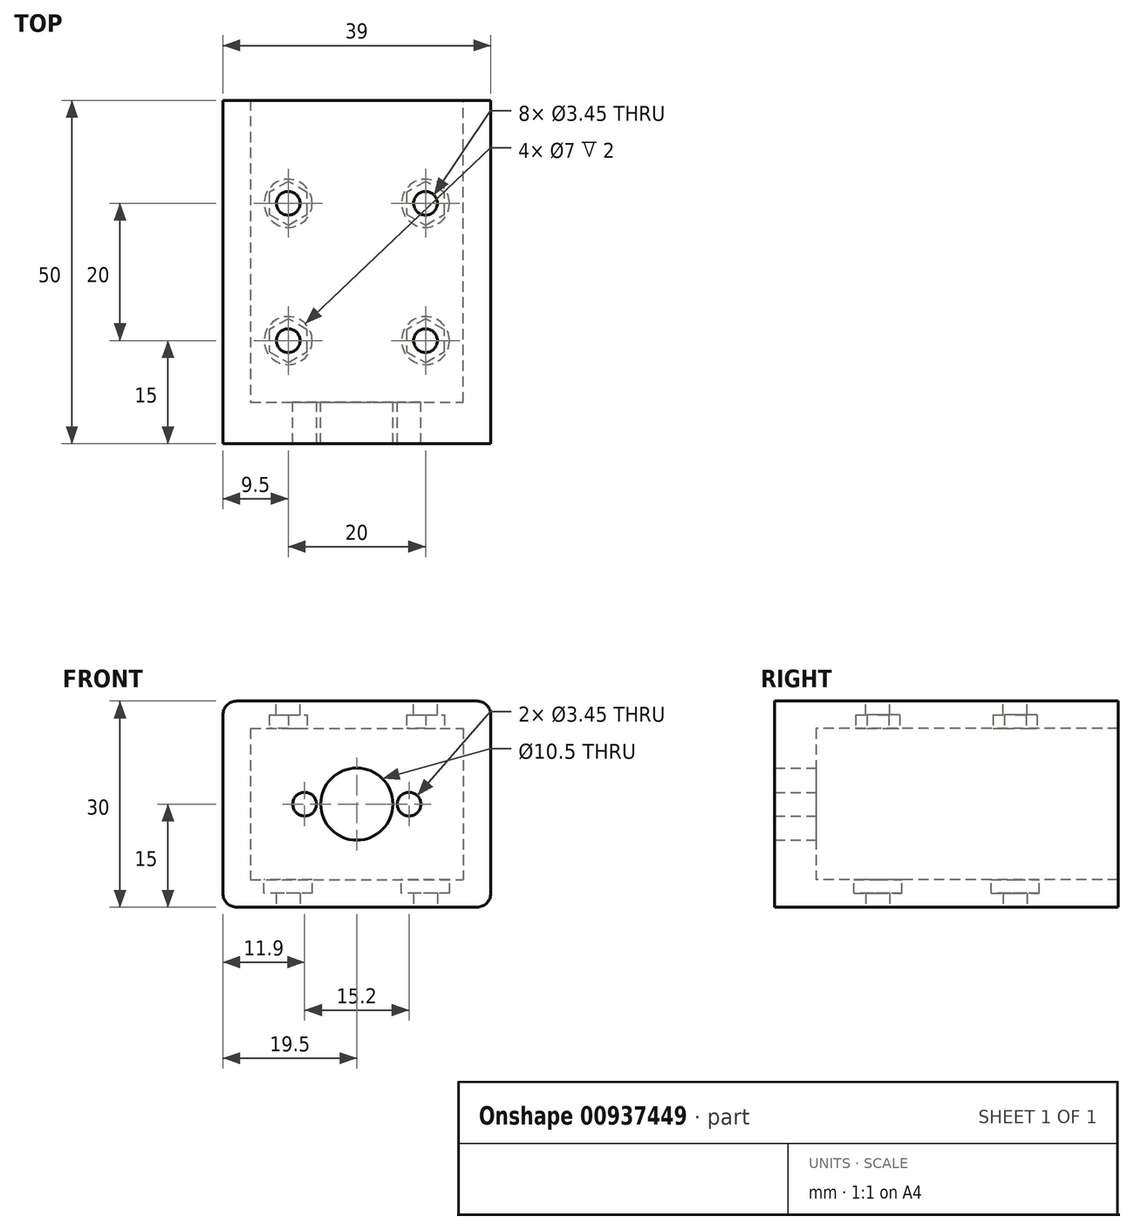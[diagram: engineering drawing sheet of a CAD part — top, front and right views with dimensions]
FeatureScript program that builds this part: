
annotation { "Feature Type Name" : "Feature", "Feature Type Description" : "" }
export const myFeature = defineFeature(function(context is Context, id is Id, definition is map)
    precondition{}
    {
        {
            var Q0;
            Q0=qCreatedBy(makeId("Top.planeOp"),FACE);
            var sketch = newSketch(context, id + "F0", { "sketchPlane" : qUnion([Q0])});
            skLineSegment(sketch, "E0.bottom", {"start": v(0, 0) * mm, "end": v(39, 0) * mm});
            skLineSegment(sketch, "E0.top", {"start": v(0, 50) * mm, "end": v(39, 50) * mm});
            skLineSegment(sketch, "E0.left", {"start": v(0, 0) * mm, "end": v(0, 50) * mm});
            skLineSegment(sketch, "E0.right", {"start": v(39, 0) * mm, "end": v(39, 50) * mm});
            skLineSegment(sketch, "E1.bottom", {"start": v(9.5, 15) * mm, "end": v(29.5, 15) * mm, "construction": true});
            skLineSegment(sketch, "E1.top", {"start": v(9.5, 35) * mm, "end": v(29.5, 35) * mm, "construction": true});
            skLineSegment(sketch, "E1.left", {"start": v(9.5, 15) * mm, "end": v(9.5, 35) * mm, "construction": true});
            skLineSegment(sketch, "E1.right", {"start": v(29.5, 15) * mm, "end": v(29.5, 35) * mm, "construction": true});
            skCircle(sketch, "E2", {"center": v(9.5, 35) * mm, "radius": 1.73 * mm});
            skCircle(sketch, "E3", {"center": v(29.5, 35) * mm, "radius": 1.73 * mm});
            skCircle(sketch, "E4", {"center": v(29.5, 15) * mm, "radius": 1.73 * mm});
            skCircle(sketch, "E5", {"center": v(9.5, 15) * mm, "radius": 1.73 * mm});
            skCircle(sketch, "E6", {"center": v(9.5, 35) * mm, "radius": 3.5 * mm});
            skCircle(sketch, "E7", {"center": v(29.5, 35) * mm, "radius": 3.5 * mm});
            skCircle(sketch, "E8", {"center": v(29.5, 15) * mm, "radius": 3.5 * mm});
            skCircle(sketch, "E9", {"center": v(9.5, 15) * mm, "radius": 3.5 * mm});
            skLineSegment(sketch, "E10", {"start": v(19.5, 0) * mm, "end": v(19.5, 15) * mm, "construction": true});
            skLineSegment(sketch, "E11", {"start": v(0, 25) * mm, "end": v(9.5, 25) * mm, "construction": true});
            skSolve(sketch);
        }
        {
            var Q0;
            Q0 = qSketchRegion(id + "F0", true);
            var Q1;
            Q1=makeQuery(id+"F0.imprint","IMPRINT",FACE,{"disambiguationData":[TD([[makeQuery(id+"F0.imprint","IMPRINT",EDGE,{"derivedFrom":sQuery(id+"F0.wireOp",EDGE,"E2")}),-1.0]])]});
            var Q2;
            Q2=makeQuery(id+"F0.imprint","IMPRINT",FACE,{"disambiguationData":[TD([[makeQuery(id+"F0.imprint","IMPRINT",EDGE,{"derivedFrom":sQuery(id+"F0.wireOp",EDGE,"E3")}),-1.0]])]});
            var Q3;
            Q3=makeQuery(id+"F0.imprint","IMPRINT",FACE,{"disambiguationData":[TD([[makeQuery(id+"F0.imprint","IMPRINT",EDGE,{"derivedFrom":sQuery(id+"F0.wireOp",EDGE,"E4")}),-1.0]])]});
            var Q4;
            Q4=makeQuery(id+"F0.imprint","IMPRINT",FACE,{"disambiguationData":[TD([[makeQuery(id+"F0.imprint","IMPRINT",EDGE,{"derivedFrom":sQuery(id+"F0.wireOp",EDGE,"E5")}),-1.0]])]});
            extrude(context, id + "F1", {"entities" : qUnion([Q0, Q1, Q2, Q3, Q4]), "depth" : 4 * mm, "offsetDistance" : 25 * mm});
        }
        {
            var Q0;
            Q0=makeQuery(id+"F1.opExtrude","CAP_FACE",FACE,{"disambiguationData":[OSD([sQuery(id+"F0.wireOp",EDGE,"E0.bottom"),sQuery(id+"F0.wireOp",EDGE,"E0.top"),sQuery(id+"F0.wireOp",EDGE,"E0.left"),sQuery(id+"F0.wireOp",EDGE,"E0.right"),sQuery(id+"F0.wireOp",EDGE,"E2"),sQuery(id+"F0.wireOp",EDGE,"E3"),sQuery(id+"F0.wireOp",EDGE,"E4"),sQuery(id+"F0.wireOp",EDGE,"E5")])],"isStart":false});
            var sketch = newSketch(context, id + "F2", { "sketchPlane" : qUnion([Q0])});
            skCircle(sketch, "E12", {"center": v(9.5, 35) * mm, "radius": 3.5 * mm});
            skCircle(sketch, "E13", {"center": v(29.5, 35) * mm, "radius": 3.5 * mm});
            skCircle(sketch, "E14", {"center": v(29.5, 15) * mm, "radius": 3.5 * mm});
            skCircle(sketch, "E15", {"center": v(9.5, 15) * mm, "radius": 3.5 * mm});
            skSolve(sketch);
        }
        {
            var Q0;
            Q0 = qSketchRegion(id + "F2", true);
            extrude(context, id + "F3", {"entities" : qUnion([Q0]), "operationType" : NewBodyOperationType.REMOVE, "oppositeDirection" : true, "depth" : 2 * mm, "offsetDistance" : 25 * mm});
        }
        {
            var Q0;
            Q0=makeQuery(id+"F1.opExtrude","CAP_FACE",FACE,{"disambiguationData":[OSD([sQuery(id+"F0.wireOp",EDGE,"E0.bottom"),sQuery(id+"F0.wireOp",EDGE,"E0.top"),sQuery(id+"F0.wireOp",EDGE,"E0.left"),sQuery(id+"F0.wireOp",EDGE,"E0.right"),sQuery(id+"F0.wireOp",EDGE,"E2"),sQuery(id+"F0.wireOp",EDGE,"E3"),sQuery(id+"F0.wireOp",EDGE,"E4"),sQuery(id+"F0.wireOp",EDGE,"E5")])],"isStart":false});
            var sketch = newSketch(context, id + "F4", { "sketchPlane" : qUnion([Q0])});
            skLineSegment(sketch, "E16", {"start": v(0, 50) * mm, "end": v(4, 50) * mm});
            skLineSegment(sketch, "E17", {"start": v(4, 50) * mm, "end": v(4, 6) * mm});
            skLineSegment(sketch, "E18", {"start": v(4, 6) * mm, "end": v(35, 6) * mm});
            skLineSegment(sketch, "E19", {"start": v(35, 6) * mm, "end": v(35, 50) * mm});
            skLineSegment(sketch, "E20", {"start": v(35, 50) * mm, "end": v(39, 50) * mm});
            skLineSegment(sketch, "E21", {"start": v(39, 50) * mm, "end": v(39, 0) * mm});
            skLineSegment(sketch, "E22", {"start": v(39, 0) * mm, "end": v(0, 0) * mm});
            skLineSegment(sketch, "E23", {"start": v(0, 0) * mm, "end": v(0, 50) * mm});
            skSolve(sketch);
        }
        {
            var Q0;
            Q0 = qSketchRegion(id + "F4", true);
            extrude(context, id + "F5", {"entities" : qUnion([Q0]), "operationType" : NewBodyOperationType.ADD, "depth" : 22 * mm, "offsetDistance" : 25 * mm});
        }
        {
            var Q0;
            Q0=makeQuery(id+"F5.opExtrude","SWEPT_FACE",FACE,{"disambiguationData":[OSD([sQuery(id+"F4.wireOp",EDGE,"E18")])]});
            var sketch = newSketch(context, id + "F6", { "sketchPlane" : qUnion([Q0])});
            skLineSegment(sketch, "E24", {"start": v(-19.5, 4) * mm, "end": v(-19.5, 15) * mm, "construction": true});
            skCircle(sketch, "E25", {"center": v(-19.5, 15) * mm, "radius": 5.25 * mm});
            skLineSegment(sketch, "E26", {"start": v(-19.5, 15) * mm, "end": v(-27.1, 15) * mm, "construction": true});
            skCircle(sketch, "E27", {"center": v(-27.1, 15) * mm, "radius": 1.73 * mm});
            skCircle(sketch, "E28", {"center": v(-11.9, 15) * mm, "radius": 1.73 * mm});
            skSolve(sketch);
        }
        {
            var Q0;
            Q0 = qSketchRegion(id + "F6", true);
            extrude(context, id + "F7", {"entities" : qUnion([Q0]), "operationType" : NewBodyOperationType.REMOVE, "endBound" : BoundingType.UP_TO_NEXT, "oppositeDirection" : true, "depth" : 25 * mm, "offsetDistance" : 25 * mm});
        }
        {
            var Q0;
            Q0=makeQuery(id+"F5.opExtrude","CAP_FACE",FACE,{"disambiguationData":[OSD([sQuery(id+"F4.wireOp",EDGE,"E16"),sQuery(id+"F4.wireOp",EDGE,"E17"),sQuery(id+"F4.wireOp",EDGE,"E18"),sQuery(id+"F4.wireOp",EDGE,"E19"),sQuery(id+"F4.wireOp",EDGE,"E20"),sQuery(id+"F4.wireOp",EDGE,"E21"),sQuery(id+"F4.wireOp",EDGE,"E22"),sQuery(id+"F4.wireOp",EDGE,"E23")])],"isStart":false});
            var sketch = newSketch(context, id + "F8", { "sketchPlane" : qUnion([Q0])});
            skLineSegment(sketch, "E29.bottom", {"start": v(0, 0) * mm, "end": v(39, 0) * mm});
            skLineSegment(sketch, "E29.top", {"start": v(0, 50) * mm, "end": v(39, 50) * mm});
            skLineSegment(sketch, "E29.left", {"start": v(0, 0) * mm, "end": v(0, 50) * mm});
            skLineSegment(sketch, "E29.right", {"start": v(39, 0) * mm, "end": v(39, 50) * mm});
            skSolve(sketch);
        }
        {
            var Q0;
            Q0 = qSketchRegion(id + "F8", true);
            extrude(context, id + "F9", {"entities" : qUnion([Q0]), "operationType" : NewBodyOperationType.ADD, "depth" : 4 * mm, "offsetDistance" : 25 * mm});
        }
        {
            var Q0;
            Q0=makeQuery(id+"F9.opExtrude","CAP_EDGE",EDGE,{"disambiguationData":[OSD([sQuery(id+"F8.wireOp",EDGE,"E29.left")])],"isStart":false});
            var Q1;
            Q1=makeQuery(id+"F1.opExtrude","CAP_EDGE",EDGE,{"disambiguationData":[OSD([sQuery(id+"F0.wireOp",EDGE,"E0.left")])],"isStart":true});
            var Q2;
            Q2=makeQuery(id+"F1.opExtrude","CAP_EDGE",EDGE,{"disambiguationData":[OSD([sQuery(id+"F0.wireOp",EDGE,"E0.right")])],"isStart":true});
            var Q3;
            Q3=makeQuery(id+"F9.opExtrude","CAP_EDGE",EDGE,{"disambiguationData":[OSD([sQuery(id+"F8.wireOp",EDGE,"E29.right")])],"isStart":false});
            var Q4;
            Q4=makeQuery(id+"F5.opExtrude","CAP_EDGE",EDGE,{"disambiguationData":[OSD([sQuery(id+"F4.wireOp",EDGE,"E19")])],"isStart":false});
            var Q5;
            Q5=makeQuery(id+"F5.opExtrude","CAP_EDGE",EDGE,{"disambiguationData":[OSD([sQuery(id+"F4.wireOp",EDGE,"E17")])],"isStart":false});
            var Q6;
            Q6=makeQuery(id+"F5.opExtrude","CAP_EDGE",EDGE,{"disambiguationData":[OSD([sQuery(id+"F4.wireOp",EDGE,"E17")])],"isStart":true});
            var Q7;
            Q7=makeQuery(id+"F5.opExtrude","CAP_EDGE",EDGE,{"disambiguationData":[OSD([sQuery(id+"F4.wireOp",EDGE,"E19")])],"isStart":true});
            fillet(context, id + "F10", {"entities" : qUnion([Q0, Q1, Q2, Q3, Q4, Q5, Q6, Q7]), "radius" : 2 * mm, "tangentPropagation" : true, "allowEdgeOverflow" : false});
        }
        {
            var Q0;
            Q0=makeQuery(id+"F9.opExtrude","CAP_FACE",FACE,{"disambiguationData":[OSD([sQuery(id+"F8.wireOp",EDGE,"E29.bottom"),sQuery(id+"F8.wireOp",EDGE,"E29.top"),sQuery(id+"F8.wireOp",EDGE,"E29.left"),sQuery(id+"F8.wireOp",EDGE,"E29.right")])],"isStart":false});
            var sketch = newSketch(context, id + "F11", { "sketchPlane" : qUnion([Q0])});
            skLineSegment(sketch, "E30.bottom", {"start": v(9.5, 35) * mm, "end": v(29.5, 35) * mm, "construction": true});
            skLineSegment(sketch, "E30.top", {"start": v(9.5, 15) * mm, "end": v(29.5, 15) * mm, "construction": true});
            skLineSegment(sketch, "E30.left", {"start": v(9.5, 35) * mm, "end": v(9.5, 15) * mm, "construction": true});
            skLineSegment(sketch, "E30.right", {"start": v(29.5, 35) * mm, "end": v(29.5, 15) * mm, "construction": true});
            skLineSegment(sketch, "E31", {"start": v(2, 25) * mm, "end": v(9.5, 25) * mm, "construction": true});
            skLineSegment(sketch, "E32", {"start": v(19.5, 15) * mm, "end": v(19.5, 0) * mm, "construction": true});
            skCircle(sketch, "E33", {"center": v(9.5, 35) * mm, "radius": 1.73 * mm});
            skCircle(sketch, "E34", {"center": v(29.5, 35) * mm, "radius": 1.73 * mm});
            skCircle(sketch, "E35", {"center": v(29.5, 15) * mm, "radius": 1.73 * mm});
            skCircle(sketch, "E36", {"center": v(9.5, 15) * mm, "radius": 1.73 * mm});
            skSolve(sketch);
        }
        {
            var Q0;
            Q0 = qSketchRegion(id + "F11", true);
            extrude(context, id + "F12", {"entities" : qUnion([Q0]), "operationType" : NewBodyOperationType.REMOVE, "endBound" : BoundingType.UP_TO_NEXT, "oppositeDirection" : true, "depth" : 25 * mm, "offsetDistance" : 25 * mm});
        }
        {
            var Q0;
            Q0=makeQuery(id+"F9.opExtrude","CAP_FACE",FACE,{"disambiguationData":[OSD([sQuery(id+"F8.wireOp",EDGE,"E29.bottom"),sQuery(id+"F8.wireOp",EDGE,"E29.top"),sQuery(id+"F8.wireOp",EDGE,"E29.left"),sQuery(id+"F8.wireOp",EDGE,"E29.right")])],"isStart":true});
            var sketch = newSketch(context, id + "F13", { "sketchPlane" : qUnion([Q0])});
            skCircle(sketch, "E37.cCircle", {"center": v(9.5, -15) * mm, "radius": 2.76 * mm, "construction": true});
            skLineSegment(sketch, "E37.0", {"start": v(9.5, -11.81) * mm, "end": v(12.26, -13.4) * mm});
            skLineSegment(sketch, "E37.1", {"start": v(12.26, -13.4) * mm, "end": v(12.26, -16.6) * mm});
            skLineSegment(sketch, "E37.2", {"start": v(12.26, -16.6) * mm, "end": v(9.5, -18.19) * mm});
            skLineSegment(sketch, "E37.3", {"start": v(9.5, -18.19) * mm, "end": v(6.74, -16.6) * mm});
            skLineSegment(sketch, "E37.4", {"start": v(6.74, -16.6) * mm, "end": v(6.74, -13.4) * mm});
            skLineSegment(sketch, "E37.5", {"start": v(6.74, -13.4) * mm, "end": v(9.5, -11.81) * mm});
            skPoint(sketch, "E37.0.midPoint", {"position": v(10.88, -12.6) * mm});
            skCircle(sketch, "E38.cCircle", {"center": v(29.5, -15) * mm, "radius": 2.76 * mm, "construction": true});
            skLineSegment(sketch, "E38.0", {"start": v(29.5, -11.81) * mm, "end": v(32.26, -13.4) * mm});
            skLineSegment(sketch, "E38.1", {"start": v(32.26, -13.4) * mm, "end": v(32.26, -16.6) * mm});
            skLineSegment(sketch, "E38.2", {"start": v(32.26, -16.6) * mm, "end": v(29.5, -18.19) * mm});
            skLineSegment(sketch, "E38.3", {"start": v(29.5, -18.19) * mm, "end": v(26.74, -16.6) * mm});
            skLineSegment(sketch, "E38.4", {"start": v(26.74, -16.6) * mm, "end": v(26.74, -13.4) * mm});
            skLineSegment(sketch, "E38.5", {"start": v(26.74, -13.4) * mm, "end": v(29.5, -11.81) * mm});
            skPoint(sketch, "E38.0.midPoint", {"position": v(30.88, -12.6) * mm});
            skCircle(sketch, "E39.cCircle", {"center": v(29.5, -35) * mm, "radius": 2.76 * mm, "construction": true});
            skLineSegment(sketch, "E39.0", {"start": v(29.5, -31.81) * mm, "end": v(32.26, -33.4) * mm});
            skLineSegment(sketch, "E39.1", {"start": v(32.26, -33.4) * mm, "end": v(32.26, -36.6) * mm});
            skLineSegment(sketch, "E39.2", {"start": v(32.26, -36.6) * mm, "end": v(29.5, -38.19) * mm});
            skLineSegment(sketch, "E39.3", {"start": v(29.5, -38.19) * mm, "end": v(26.74, -36.6) * mm});
            skLineSegment(sketch, "E39.4", {"start": v(26.74, -36.6) * mm, "end": v(26.74, -33.4) * mm});
            skLineSegment(sketch, "E39.5", {"start": v(26.74, -33.4) * mm, "end": v(29.5, -31.81) * mm});
            skPoint(sketch, "E39.0.midPoint", {"position": v(30.88, -32.6) * mm});
            skCircle(sketch, "E40.cCircle", {"center": v(9.5, -35) * mm, "radius": 2.76 * mm, "construction": true});
            skLineSegment(sketch, "E40.0", {"start": v(9.5, -31.81) * mm, "end": v(12.26, -33.4) * mm});
            skLineSegment(sketch, "E40.1", {"start": v(12.26, -33.4) * mm, "end": v(12.26, -36.6) * mm});
            skLineSegment(sketch, "E40.2", {"start": v(12.26, -36.6) * mm, "end": v(9.5, -38.19) * mm});
            skLineSegment(sketch, "E40.3", {"start": v(9.5, -38.19) * mm, "end": v(6.74, -36.6) * mm});
            skLineSegment(sketch, "E40.4", {"start": v(6.74, -36.6) * mm, "end": v(6.74, -33.4) * mm});
            skLineSegment(sketch, "E40.5", {"start": v(6.74, -33.4) * mm, "end": v(9.5, -31.81) * mm});
            skPoint(sketch, "E40.0.midPoint", {"position": v(10.88, -32.6) * mm});
            skSolve(sketch);
        }
        {
            var Q0;
            Q0 = qSketchRegion(id + "F13", true);
            extrude(context, id + "F14", {"entities" : qUnion([Q0]), "operationType" : NewBodyOperationType.REMOVE, "oppositeDirection" : true, "depth" : 2 * mm, "offsetDistance" : 25 * mm});
        }
    });
